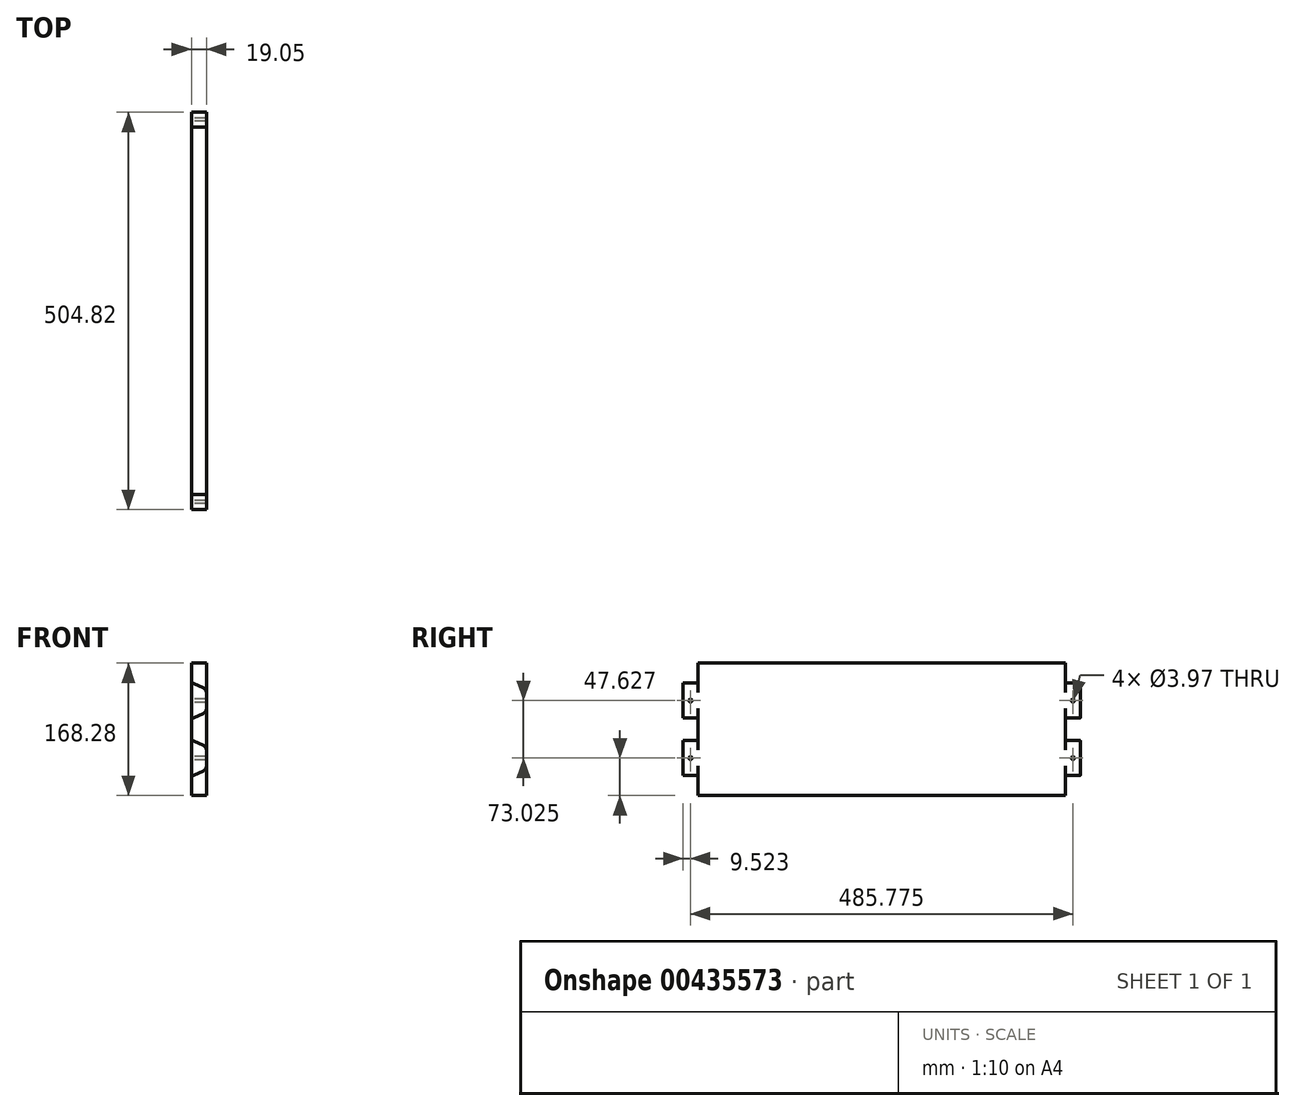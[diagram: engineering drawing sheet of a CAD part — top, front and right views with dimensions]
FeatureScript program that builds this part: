
annotation { "Feature Type Name" : "Feature", "Feature Type Description" : "" }
export const myFeature = defineFeature(function(context is Context, id is Id, definition is map)
    precondition{}
    {
        {
            var Q0;
            Q0=qCreatedBy(makeId("Right.planeOp"),FACE);
            var sketch = newSketch(context, id + "F0", { "sketchPlane" : qUnion([Q0])});
            skLineSegment(sketch, "E0.bottom", {"start": v(252.41, -84.14) * mm, "end": v(-252.41, -84.14) * mm});
            skLineSegment(sketch, "E0.top", {"start": v(252.41, 84.14) * mm, "end": v(-252.41, 84.14) * mm});
            skLineSegment(sketch, "E0.left", {"start": v(252.41, -84.14) * mm, "end": v(252.41, 84.14) * mm});
            skLineSegment(sketch, "E0.right", {"start": v(-252.41, -84.14) * mm, "end": v(-252.41, 84.14) * mm});
            skPoint(sketch, "E0.middle", {"position": v(0, 0) * mm});
            skSolve(sketch);
        }
        {
            var Q0;
            Q0=makeQuery(id+"F0.imprint","IMPRINT",FACE,{"disambiguationData":[TD([[makeQuery(id+"F0.imprint","IMPRINT",EDGE,{"derivedFrom":sQuery(id+"F0.wireOp",EDGE,"E0.bottom")}),-1.0]])]});
            extrude(context, id + "F1", {"entities" : qUnion([Q0]), "depth" : 19.05 * mm, "offsetDistance" : 25.4 * mm});
        }
        {
            var Q0;
            Q0=makeQuery(id+"F1.opExtrude","SWEPT_FACE",FACE,{"disambiguationData":[OSD([sQuery(id+"F0.wireOp",EDGE,"E0.right")])]});
            var sketch = newSketch(context, id + "F2", { "sketchPlane" : qUnion([Q0])});
            skLineSegment(sketch, "E1.MirrorCS", {"start": v(0.21, 58.74) * mm, "end": v(0, 58.74) * mm});
            skArc(sketch, "E2.MirrorCS", {"start": v(2.84, 58.17) * mm, "mid": v(1.56, 58.6) * mm, "end": v(0.21, 58.74) * mm});
            skArc(sketch, "E3.MirrorCS", {"start": v(0.21, 14.29) * mm, "mid": v(1.56, 14.43) * mm, "end": v(2.84, 14.86) * mm});
            skLineSegment(sketch, "E4.MirrorCS", {"start": v(0, 14.29) * mm, "end": v(0.21, 14.29) * mm});
            skArc(sketch, "E5.MirrorCS", {"start": v(15.33, 20.53) * mm, "mid": v(18.04, 22.88) * mm, "end": v(19.05, 26.31) * mm});
            skLineSegment(sketch, "E6.MirrorCS", {"start": v(2.84, 14.86) * mm, "end": v(15.33, 20.53) * mm});
            skLineSegment(sketch, "E7.MirrorCS", {"start": v(19.05, 26.31) * mm, "end": v(19.05, 46.71) * mm});
            skLineSegment(sketch, "E8.MirrorCS", {"start": v(15.33, 52.5) * mm, "end": v(2.84, 58.17) * mm});
            skArc(sketch, "E9.MirrorCS", {"start": v(19.05, 46.71) * mm, "mid": v(18.04, 50.15) * mm, "end": v(15.33, 52.5) * mm});
            skLineSegment(sketch, "E10.MirrorCS", {"start": v(0, -14.29) * mm, "end": v(0.21, -14.29) * mm});
            skLineSegment(sketch, "E11.MirrorCS", {"start": v(0.21, -58.74) * mm, "end": v(0, -58.74) * mm});
            skArc(sketch, "E12.MirrorCS", {"start": v(0.21, -14.29) * mm, "mid": v(1.56, -14.43) * mm, "end": v(2.84, -14.86) * mm});
            skArc(sketch, "E13.MirrorCS", {"start": v(2.84, -58.17) * mm, "mid": v(1.56, -58.6) * mm, "end": v(0.21, -58.74) * mm});
            skLineSegment(sketch, "E14.MirrorCS", {"start": v(19.05, -26.31) * mm, "end": v(19.05, -46.71) * mm});
            skLineSegment(sketch, "E15.MirrorCS", {"start": v(2.84, -14.86) * mm, "end": v(15.33, -20.53) * mm});
            skArc(sketch, "E16.MirrorCS", {"start": v(19.05, -46.71) * mm, "mid": v(18.04, -50.15) * mm, "end": v(15.33, -52.5) * mm});
            skLineSegment(sketch, "E17.MirrorCS", {"start": v(15.33, -52.5) * mm, "end": v(2.84, -58.17) * mm});
            skArc(sketch, "E18.MirrorCS", {"start": v(15.33, -20.53) * mm, "mid": v(18.04, -22.88) * mm, "end": v(19.05, -26.31) * mm});
            skSolve(sketch);
        }
        {
            var Q0;
            Q0=makeQuery(id+"F1.opExtrude","SWEPT_FACE",FACE,{"disambiguationData":[OSD([sQuery(id+"F0.wireOp",EDGE,"E0.left")])]});
            var sketch = newSketch(context, id + "F3", { "sketchPlane" : qUnion([Q0])});
            skLineSegment(sketch, "E19.left", {"start": v(0, -84.14) * mm, "end": v(0, 84.14) * mm});
            skLineSegment(sketch, "E20.MirrorCS", {"start": v(-0.21, -58.74) * mm, "end": v(0, -58.74) * mm});
            skArc(sketch, "E21.MirrorCS", {"start": v(-2.84, -58.17) * mm, "mid": v(-1.56, -58.6) * mm, "end": v(-0.21, -58.74) * mm});
            skArc(sketch, "E22.MirrorCS", {"start": v(-0.21, -14.29) * mm, "mid": v(-1.56, -14.43) * mm, "end": v(-2.84, -14.86) * mm});
            skLineSegment(sketch, "E23.MirrorCS", {"start": v(0, -14.29) * mm, "end": v(-0.21, -14.29) * mm});
            skArc(sketch, "E24.MirrorCS", {"start": v(-15.33, -20.53) * mm, "mid": v(-18.04, -22.88) * mm, "end": v(-19.05, -26.31) * mm});
            skLineSegment(sketch, "E25.MirrorCS", {"start": v(-2.84, -14.86) * mm, "end": v(-15.33, -20.53) * mm});
            skLineSegment(sketch, "E26.MirrorCS", {"start": v(-19.05, -26.31) * mm, "end": v(-19.05, -46.71) * mm});
            skLineSegment(sketch, "E27.MirrorCS", {"start": v(-15.33, -52.5) * mm, "end": v(-2.84, -58.17) * mm});
            skArc(sketch, "E28.MirrorCS", {"start": v(-19.05, -46.71) * mm, "mid": v(-18.04, -50.15) * mm, "end": v(-15.33, -52.5) * mm});
            skLineSegment(sketch, "E29.MirrorCS", {"start": v(0, 14.29) * mm, "end": v(-0.21, 14.29) * mm});
            skLineSegment(sketch, "E30.MirrorCS", {"start": v(-0.21, 58.74) * mm, "end": v(0, 58.74) * mm});
            skArc(sketch, "E31.MirrorCS", {"start": v(-0.21, 14.29) * mm, "mid": v(-1.56, 14.43) * mm, "end": v(-2.84, 14.86) * mm});
            skArc(sketch, "E32.MirrorCS", {"start": v(-2.84, 58.17) * mm, "mid": v(-1.56, 58.6) * mm, "end": v(-0.21, 58.74) * mm});
            skLineSegment(sketch, "E33.MirrorCS", {"start": v(-19.05, 26.31) * mm, "end": v(-19.05, 46.71) * mm});
            skLineSegment(sketch, "E34.MirrorCS", {"start": v(-2.84, 14.86) * mm, "end": v(-15.33, 20.53) * mm});
            skArc(sketch, "E35.MirrorCS", {"start": v(-19.05, 46.71) * mm, "mid": v(-18.04, 50.15) * mm, "end": v(-15.33, 52.5) * mm});
            skLineSegment(sketch, "E36.MirrorCS", {"start": v(-15.33, 52.5) * mm, "end": v(-2.84, 58.17) * mm});
            skArc(sketch, "E37.MirrorCS", {"start": v(-15.33, 20.53) * mm, "mid": v(-18.04, 22.88) * mm, "end": v(-19.05, 26.31) * mm});
            skSolve(sketch);
        }
        {
            var Q0;
            {var subQ1=sQuery(id+"F3.wireOp",EDGE,"E30.MirrorCS");Q0=makeQuery(id+"F3.imprint","IMPRINT",FACE,{"disambiguationData":[TD([[makeQuery(id+"F3.imprint","IMPRINT",EDGE,{"derivedFrom":subQ1}),1.0]])]});}
            var Q1;
            Q1=makeQuery(id+"F3.imprint","IMPRINT",FACE,{"disambiguationData":[TD([[makeQuery(id+"F3.imprint","IMPRINT",EDGE,{"derivedFrom":sQuery(id+"F3.wireOp",EDGE,"E22.MirrorCS")}),-1.0]])]});
            var Q2;
            {var subQ3=sQuery(id+"F3.wireOp",EDGE,"E20.MirrorCS");Q2=makeQuery(id+"F3.imprint","IMPRINT",FACE,{"disambiguationData":[TD([[makeQuery(id+"F3.imprint","IMPRINT",EDGE,{"derivedFrom":subQ3}),-1.0]])]});}
            var Q3;
            {var subQ1=sQuery(id+"F2.wireOp",EDGE,"E11.MirrorCS");Q3=makeQuery(id+"F2.imprint","IMPRINT",FACE,{"disambiguationData":[TD([[makeQuery(id+"F2.imprint","IMPRINT",EDGE,{"derivedFrom":subQ1}),1.0]])]});}
            extrude(context, id + "F4", {"entities" : qUnion([Q0, Q1, Q2, Q3]), "operationType" : NewBodyOperationType.REMOVE, "oppositeDirection" : true, "depth" : 19.05 * mm, "offsetDistance" : 25.4 * mm});
        }
        {
            var Q0;
            Q0=makeQuery(id+"F2.imprint","IMPRINT",FACE,{"disambiguationData":[TD([[makeQuery(id+"F2.imprint","IMPRINT",EDGE,{"derivedFrom":sQuery(id+"F2.wireOp",EDGE,"E3.MirrorCS")}),-1.0]])]});
            var Q1;
            {var subQ3=sQuery(id+"F2.wireOp",EDGE,"E1.MirrorCS");Q1=makeQuery(id+"F2.imprint","IMPRINT",FACE,{"disambiguationData":[TD([[makeQuery(id+"F2.imprint","IMPRINT",EDGE,{"derivedFrom":subQ3}),-1.0]])]});}
            var Q2;
            {var subQ1=sQuery(id+"F2.wireOp",EDGE,"E11.MirrorCS");Q2=makeQuery(id+"F2.imprint","IMPRINT",FACE,{"disambiguationData":[TD([[makeQuery(id+"F2.imprint","IMPRINT",EDGE,{"derivedFrom":subQ1}),1.0]])]});}
            extrude(context, id + "F5", {"entities" : qUnion([Q0, Q1, Q2]), "operationType" : NewBodyOperationType.REMOVE, "oppositeDirection" : true, "depth" : 19.05 * mm, "offsetDistance" : 25.4 * mm});
        }
        {
            var Q0;
            Q0=makeQuery(id+"F1.opExtrude","CAP_FACE",FACE,{"disambiguationData":[OSD([sQuery(id+"F0.wireOp",EDGE,"E0.bottom"),sQuery(id+"F0.wireOp",EDGE,"E0.top"),sQuery(id+"F0.wireOp",EDGE,"E0.left"),sQuery(id+"F0.wireOp",EDGE,"E0.right")])],"isStart":true});
            var sketch = newSketch(context, id + "F6", { "sketchPlane" : qUnion([Q0])});
            skCircle(sketch, "E38", {"center": v(-242.89, -36.51) * mm, "radius": 1.98 * mm});
            skPoint(sketch, "E38.centerSnap0", {"position": v(-242.89, -14.29) * mm});
            skPoint(sketch, "E38.centerSnap1", {"position": v(-252.41, -36.51) * mm});
            skCircle(sketch, "E39", {"center": v(-242.89, 36.51) * mm, "radius": 1.98 * mm});
            skPoint(sketch, "E40", {"position": v(-252.41, 36.51) * mm});
            skPoint(sketch, "E41", {"position": v(-242.89, 58.74) * mm});
            skCircle(sketch, "E42", {"center": v(242.89, -36.51) * mm, "radius": 1.98 * mm});
            skCircle(sketch, "E43", {"center": v(242.89, 36.51) * mm, "radius": 1.98 * mm});
            skPoint(sketch, "E44", {"position": v(242.89, -58.74) * mm});
            skPoint(sketch, "E45", {"position": v(252.41, -36.51) * mm});
            skSolve(sketch);
        }
        {
            var Q0;
            Q0=makeQuery(id+"F6.imprint","IMPRINT",FACE,{"disambiguationData":[TD([[makeQuery(id+"F6.imprint","IMPRINT",EDGE,{"derivedFrom":sQuery(id+"F6.wireOp",EDGE,"E39")}),1.0]])]});
            var Q1;
            Q1=makeQuery(id+"F6.imprint","IMPRINT",FACE,{"disambiguationData":[TD([[makeQuery(id+"F6.imprint","IMPRINT",EDGE,{"derivedFrom":sQuery(id+"F6.wireOp",EDGE,"E38")}),1.0]])]});
            var Q2;
            Q2=makeQuery(id+"F6.imprint","IMPRINT",FACE,{"disambiguationData":[TD([[makeQuery(id+"F6.imprint","IMPRINT",EDGE,{"derivedFrom":sQuery(id+"F6.wireOp",EDGE,"E42")}),1.0]])]});
            var Q3;
            Q3=makeQuery(id+"F6.imprint","IMPRINT",FACE,{"disambiguationData":[TD([[makeQuery(id+"F6.imprint","IMPRINT",EDGE,{"derivedFrom":sQuery(id+"F6.wireOp",EDGE,"E43")}),1.0]])]});
            extrude(context, id + "F7", {"entities" : qUnion([Q0, Q1, Q2, Q3]), "operationType" : NewBodyOperationType.REMOVE, "oppositeDirection" : true, "depth" : 19.05 * mm, "offsetDistance" : 25.4 * mm});
        }
    });
